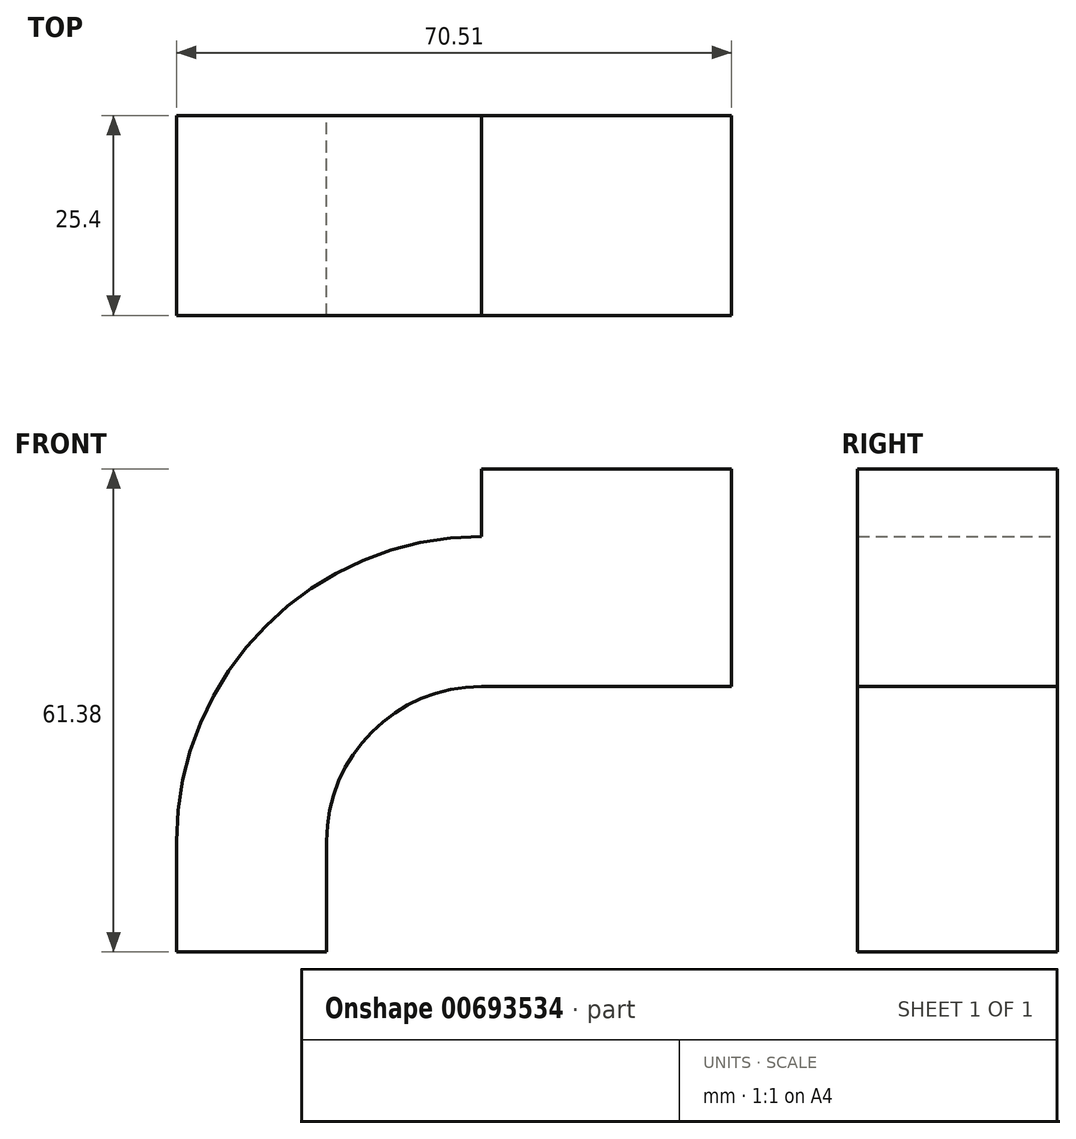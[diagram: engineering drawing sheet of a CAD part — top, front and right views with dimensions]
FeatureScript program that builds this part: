
annotation { "Feature Type Name" : "Feature", "Feature Type Description" : "" }
export const myFeature = defineFeature(function(context is Context, id is Id, definition is map)
    precondition{}
    {
        {
            var Q0;
            Q0=qCreatedBy(makeId("Front.planeOp"),FACE);
            var sketch = newSketch(context, id + "F0", { "sketchPlane" : qUnion([Q0])});
            skLineSegment(sketch, "E0.bottom", {"start": v(51.62, 21.97) * mm, "end": v(-30.93, 21.97) * mm});
            skLineSegment(sketch, "E0.top", {"start": v(51.62, 2.92) * mm, "end": v(-30.93, 2.92) * mm});
            skLineSegment(sketch, "E0.left", {"start": v(51.62, 21.97) * mm, "end": v(51.62, 2.92) * mm});
            skLineSegment(sketch, "E0.right", {"start": v(-30.93, 21.97) * mm, "end": v(-30.93, 2.92) * mm});
            skPoint(sketch, "E0.middle", {"position": v(10.34, 12.44) * mm});
            skLineSegment(sketch, "E1.bottom", {"start": v(88.63, 55.71) * mm, "end": v(56.86, 55.71) * mm});
            skLineSegment(sketch, "E1.top", {"start": v(88.63, 83.35) * mm, "end": v(56.86, 83.35) * mm});
            skLineSegment(sketch, "E1.left", {"start": v(88.63, 55.71) * mm, "end": v(88.63, 83.35) * mm});
            skLineSegment(sketch, "E1.right", {"start": v(56.86, 55.71) * mm, "end": v(56.86, 83.35) * mm});
            skPoint(sketch, "E1.middle", {"position": v(72.74, 69.53) * mm});
            skLineSegment(sketch, "E2", {"start": v(37.17, 21.97) * mm, "end": v(37.17, 36.02) * mm});
            skArc(sketch, "E3", {"start": v(37.17, 36.02) * mm, "mid": v(42.93, 49.94) * mm, "end": v(56.86, 55.71) * mm});
            skArc(sketch, "E4.0", {"start": v(18.12, 36.02) * mm, "mid": v(29.46, 63.41) * mm, "end": v(56.86, 74.76) * mm});
            skLineSegment(sketch, "E4.1", {"start": v(18.12, 21.97) * mm, "end": v(18.12, 36.02) * mm});
            skArc(sketch, "E5", {"start": v(56.86, 74.76) * mm, "mid": v(4.67, 62.14) * mm, "end": v(-30.93, 21.97) * mm});
            skSolve(sketch);
        }
        {
            var Q0;
            {var subQ1=sQuery(id+"F0.wireOp",EDGE,"E1.bottom");Q0=makeQuery(id+"F0.imprint","IMPRINT",FACE,{"disambiguationData":[TD([[makeQuery(id+"F0.imprint","IMPRINT",EDGE,{"derivedFrom":subQ1}),-1.0]])]});}
            var Q1;
            Q1=makeQuery(id+"F0.imprint","IMPRINT",FACE,{"disambiguationData":[TD([[makeQuery(id+"F0.imprint","IMPRINT",EDGE,{"derivedFrom":sQuery(id+"F0.wireOp",EDGE,"E4.0")}),1.0]])]});
            var Q2;
            {var subQ1=sQuery(id+"F0.wireOp",EDGE,"E2");Q2=makeQuery(id+"F0.imprint","IMPRINT",FACE,{"disambiguationData":[TD([[makeQuery(id+"F0.imprint","IMPRINT",EDGE,{"derivedFrom":subQ1}),1.0]])]});}
            extrude(context, id + "F1", {"entities" : qUnion([Q0, Q1, Q2]), "depth" : 25.4 * mm, "offsetDistance" : 25.4 * mm});
        }
    });
